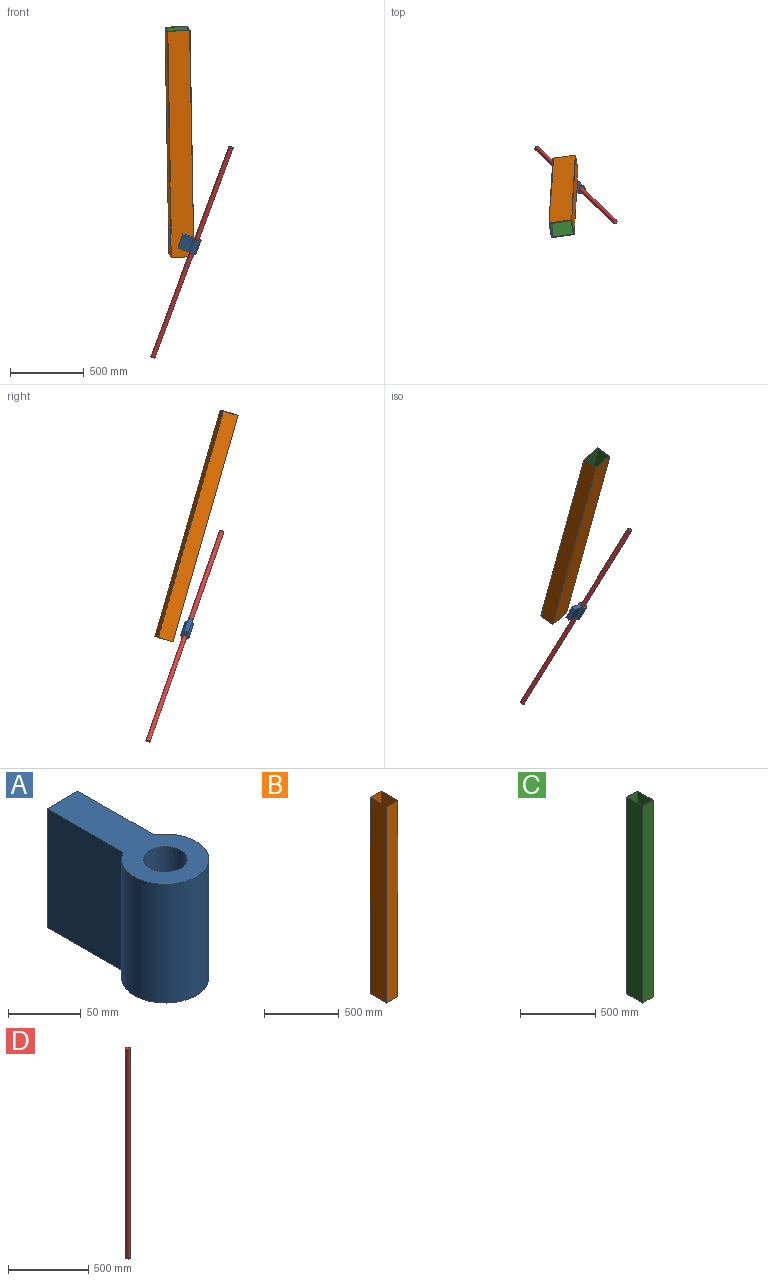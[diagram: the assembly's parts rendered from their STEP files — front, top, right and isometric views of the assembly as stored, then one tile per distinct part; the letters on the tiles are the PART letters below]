
ASSEMBLY  parts=4 mates=2
PART A: 7 faces, bbox 60x130x100 mm
  f0: cylinder r=30mm len=100mm, axis (0,0,1), area 15708mm2, adj f1,f4,f5,f6
  f1: plane 100x74.02mm, normal (1,0,0), area 7401.9mm2, adj f0,f2,f5,f6
  f2: plane 100x30mm, normal (0,1,0), area 3000mm2, adj f1,f4,f5,f6
  f3: cylinder r=15.05mm len=100mm, axis (0,0,1), area 9456.2mm2, adj f5,f6
  f4: plane 100x74.02mm, normal (-1,0,0), area 7401.9mm2, adj f0,f2,f5,f6
  f5: plane 130x60mm, normal (0,0,-1), area 4254.9mm2, adj f0,f1,f2,f3,f4
  f6: plane 130x60mm, normal (0,0,1), area 4254.9mm2, adj f0,f1,f2,f3,f4
PART B: 10 faces, bbox 106x156x1600 mm
  f0: plane 1600x106mm, normal (0,-1,0), area 169600mm2, adj f1,f7,f8,f9
  f1: plane 1600x156mm, normal (1,0,0), area 249600mm2, adj f0,f2,f8,f9
  f2: plane 1600x106mm, normal (0,1,0), area 169600mm2, adj f1,f7,f8,f9
  f3: plane 1600x151mm, normal (-1,0,0), area 241600mm2, adj f4,f6,f8,f9
  f4: plane 1600x101mm, normal (0,1,0), area 161600mm2, adj f3,f5,f8,f9
  f5: plane 1600x151mm, normal (1,0,0), area 241600mm2, adj f4,f6,f8,f9
  f6: plane 1600x101mm, normal (0,-1,0), area 161600mm2, adj f3,f5,f8,f9
  f7: plane 1600x156mm, normal (-1,0,0), area 249600mm2, adj f0,f2,f8,f9
  f8: plane 156x106mm, normal (0,0,1), area 1285mm2, adj f0,f1,f2,f3,f4,f5,f6,f7
  f9: plane 156x106mm, normal (0,0,-1), area 1285mm2, adj f0,f1,f2,f3,f4,f5,f6,f7
PART C: 10 faces, bbox 100x150x1600 mm
  f0: plane 1600x100mm, normal (0,-1,0), area 160000mm2, adj f1,f7,f8,f9
  f1: plane 1600x150mm, normal (1,0,0), area 240000mm2, adj f0,f2,f8,f9
  f2: plane 1600x100mm, normal (0,1,0), area 160000mm2, adj f1,f7,f8,f9
  f3: plane 1600x145mm, normal (-1,0,0), area 232000mm2, adj f4,f6,f8,f9
  f4: plane 1600x95mm, normal (0,1,0), area 152000mm2, adj f3,f5,f8,f9
  f5: plane 1600x145mm, normal (1,0,0), area 232000mm2, adj f4,f6,f8,f9
  f6: plane 1600x95mm, normal (0,-1,0), area 152000mm2, adj f3,f5,f8,f9
  f7: plane 1600x150mm, normal (-1,0,0), area 240000mm2, adj f0,f2,f8,f9
  f8: plane 150x100mm, normal (0,0,1), area 1225mm2, adj f0,f1,f2,f3,f4,f5,f6,f7
  f9: plane 150x100mm, normal (0,0,-1), area 1225mm2, adj f0,f1,f2,f3,f4,f5,f6,f7
PART D: 3 faces, bbox 30x30x1600 mm
  f0: cylinder r=15mm len=1600mm, axis (0,0,-1), area 150796.4mm2, adj f1,f2
  f1: plane 30x30mm, normal (0,0,1), area 706.9mm2, adj f0
  f2: plane 30x30mm, normal (0,0,-1), area 706.9mm2, adj f0
PLACE A rot(axis=(0.32,0,0.95),96deg) t=(-547.15,-600.47,-2467.3)mm
PLACE B rot(axis=(0.11,-0.15,0.98),99.4deg) t=(-652.42,-427.17,-2575.64)mm
PLACE C rot(axis=(0.11,-0.15,0.98),99.4deg) t=(-651.85,-427.58,-2575.75)mm
PLACE D rot(axis=(-0.17,0.17,-0.97),177.1deg) t=(-845.17,-318.7,-3268.41)mm
MATE slider B.f9 <-> C.f9  axis (0.02,0.28,-0.96) through (-570.22,-464.66,-2585.03)mm
MATE slider A.f0 <-> D.f0  axis (0.33,-0.31,0.89) through (-580.26,-569.16,-2556.31)mm
